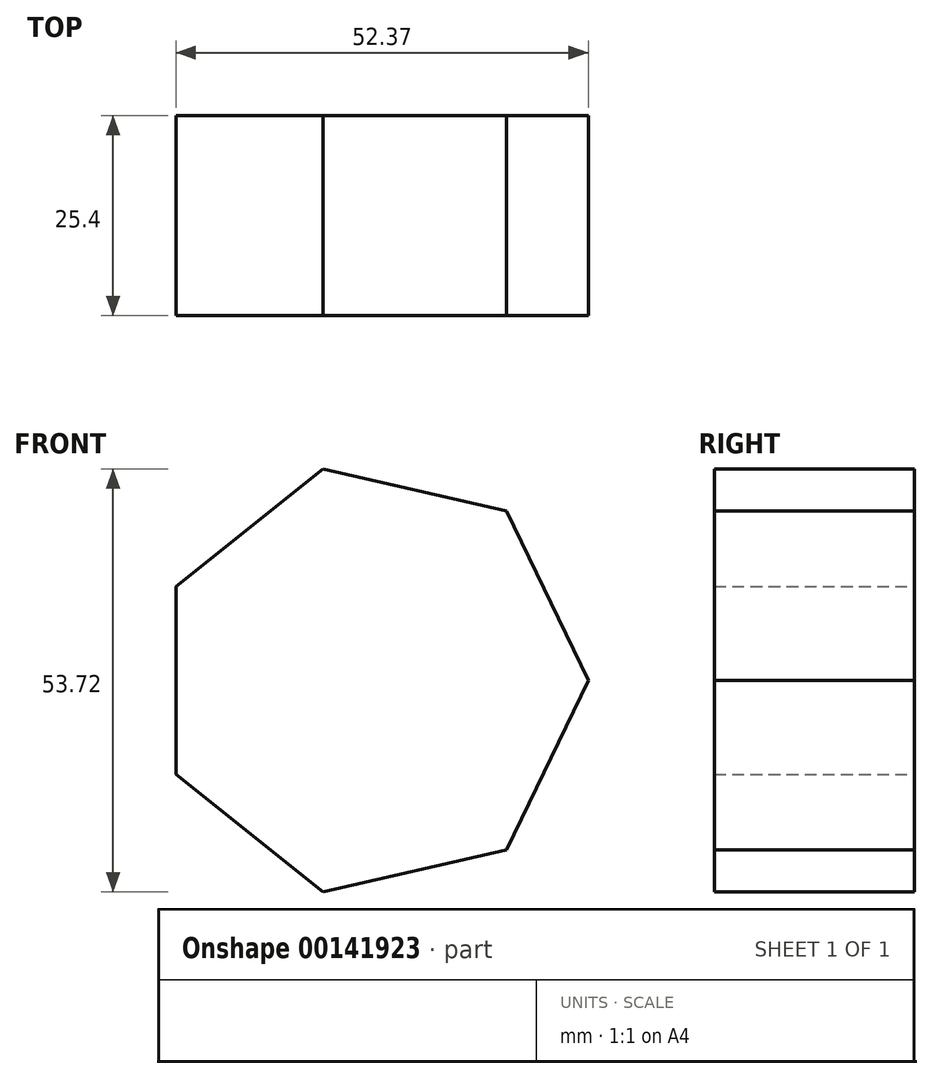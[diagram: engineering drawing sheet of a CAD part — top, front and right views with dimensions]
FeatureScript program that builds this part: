
annotation { "Feature Type Name" : "Feature", "Feature Type Description" : "" }
export const myFeature = defineFeature(function(context is Context, id is Id, definition is map)
    precondition{}
    {
        {
            var Q0;
            Q0=qCreatedBy(makeId("Front.planeOp"),FACE);
            var sketch = newSketch(context, id + "F0", { "sketchPlane" : qUnion([Q0])});
            skCircle(sketch, "E0.cCircle", {"center": v(0, 0) * mm, "radius": 24.82 * mm, "construction": true});
            skLineSegment(sketch, "E0.0", {"start": v(-24.82, -11.95) * mm, "end": v(-24.82, 11.95) * mm});
            skLineSegment(sketch, "E0.1", {"start": v(-24.82, 11.95) * mm, "end": v(-6.13, 26.86) * mm});
            skLineSegment(sketch, "E0.2", {"start": v(-6.13, 26.86) * mm, "end": v(17.18, 21.54) * mm});
            skLineSegment(sketch, "E0.3", {"start": v(17.18, 21.54) * mm, "end": v(27.55, 0) * mm});
            skLineSegment(sketch, "E0.4", {"start": v(27.55, 0) * mm, "end": v(17.18, -21.54) * mm});
            skLineSegment(sketch, "E0.5", {"start": v(17.18, -21.54) * mm, "end": v(-6.13, -26.86) * mm});
            skLineSegment(sketch, "E0.6", {"start": v(-6.13, -26.86) * mm, "end": v(-24.82, -11.95) * mm});
            skPoint(sketch, "E0.0.midPoint", {"position": v(-24.82, 0) * mm});
            skSolve(sketch);
        }
        {
            var Q0;
            Q0=qSketchRegion(id+"F0",true);
            extrude(context, id + "F1", {"entities" : qUnion([Q0]), "depth" : 25.4 * mm});
        }
    });
